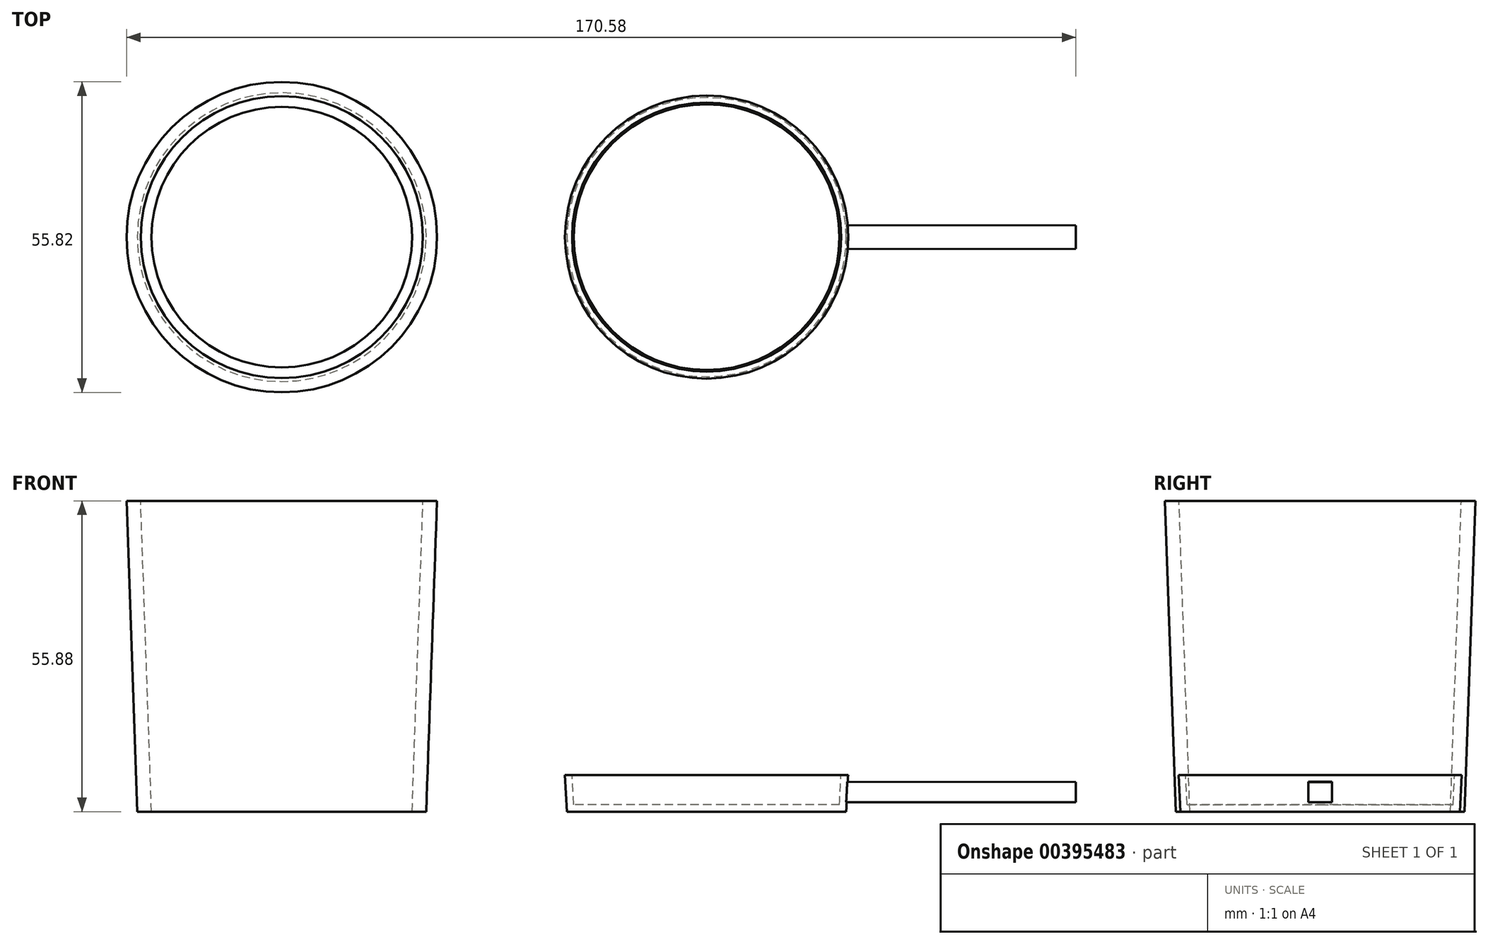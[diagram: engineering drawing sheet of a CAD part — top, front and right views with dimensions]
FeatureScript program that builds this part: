
annotation { "Feature Type Name" : "Feature", "Feature Type Description" : "" }
export const myFeature = defineFeature(function(context is Context, id is Id, definition is map)
    precondition{}
    {
        {
            var Q0;
            Q0=qCreatedBy(makeId("Top.planeOp"),FACE);
            var sketch = newSketch(context, id + "F0", { "sketchPlane" : qUnion([Q0])});
            skCircle(sketch, "E0", {"center": v(35, 0) * mm, "radius": 25.1 * mm});
            skSolve(sketch);
        }
        {
            var Q0;
            Q0 = qSketchRegion(id + "F0", true);
            extrude(context, id + "F1", {"entities" : qUnion([Q0]), "depth" : 6.6 * mm, "hasDraft" : true, "draftAngle" : 3 * degree});
        }
        {
            var Q0;
            Q0=makeQuery(id+"F1.opExtrude","CAP_FACE",FACE,{"disambiguationData":[OSD([sQuery(id+"F0.wireOp",EDGE,"E0")])],"isStart":false});
            shell(context, id + "F2", {"entities" : qUnion([Q0]), "thickness" : 1.27 * mm});
        }
        {
            var Q0;
            Q0=qCreatedBy(makeId("Right.planeOp"),FACE);
            cPlane(context, id + "F3", {"entities" : qUnion([Q0]), "cplaneType" : CPlaneType.OFFSET, "offset" : 59.94 * mm, "width" : 152.4 * mm, "height" : 152.4 * mm});
        }
        {
            var Q0;
            Q0=qCreatedBy(id+"F3.planeOp",FACE);
            var sketch = newSketch(context, id + "F4", { "sketchPlane" : qUnion([Q0])});
            skLineSegment(sketch, "E1.bottom", {"start": v(-2.14, 1.68) * mm, "end": v(2.14, 1.68) * mm});
            skLineSegment(sketch, "E1.top", {"start": v(-2.14, 5.37) * mm, "end": v(2.14, 5.37) * mm});
            skLineSegment(sketch, "E1.left", {"start": v(-2.14, 1.68) * mm, "end": v(-2.14, 5.37) * mm});
            skLineSegment(sketch, "E1.right", {"start": v(2.14, 1.68) * mm, "end": v(2.14, 5.37) * mm});
            skPoint(sketch, "E1.middle", {"position": v(0, 3.52) * mm});
            skSolve(sketch);
        }
        {
            var Q0;
            Q0 = qSketchRegion(id + "F4", true);
            extrude(context, id + "F5", {"entities" : qUnion([Q0]), "operationType" : NewBodyOperationType.ADD, "depth" : 41.4 * mm, "hasDraft" : true, "draftAngle" : 0.05 * degree, "draftPullDirection" : true});
        }
        {
            var Q0;
            Q0=qCreatedBy(makeId("Top.planeOp"),FACE);
            var sketch = newSketch(context, id + "F6", { "sketchPlane" : qUnion([Q0])});
            skCircle(sketch, "E2", {"center": v(-41.33, 0) * mm, "radius": 25.95 * mm});
            skSolve(sketch);
        }
        {
            var Q0;
            Q0 = qSketchRegion(id + "F6", true);
            extrude(context, id + "F7", {"entities" : qUnion([Q0]), "depth" : 55.88 * mm, "hasDraft" : true, "draftAngle" : 2 * degree});
        }
        {
            var Q0;
            Q0=makeQuery(id+"F7.opExtrude","CAP_FACE",FACE,{"disambiguationData":[OSD([sQuery(id+"F6.wireOp",EDGE,"E2")])],"isStart":false});
            var Q1;
            Q1=makeQuery(id+"F7.opExtrude","CAP_FACE",FACE,{"disambiguationData":[OSD([sQuery(id+"F6.wireOp",EDGE,"E2")])],"isStart":true});
            shell(context, id + "F8", {"entities" : qUnion([Q0, Q1]), "thickness" : 2.54 * mm});
        }
    });
